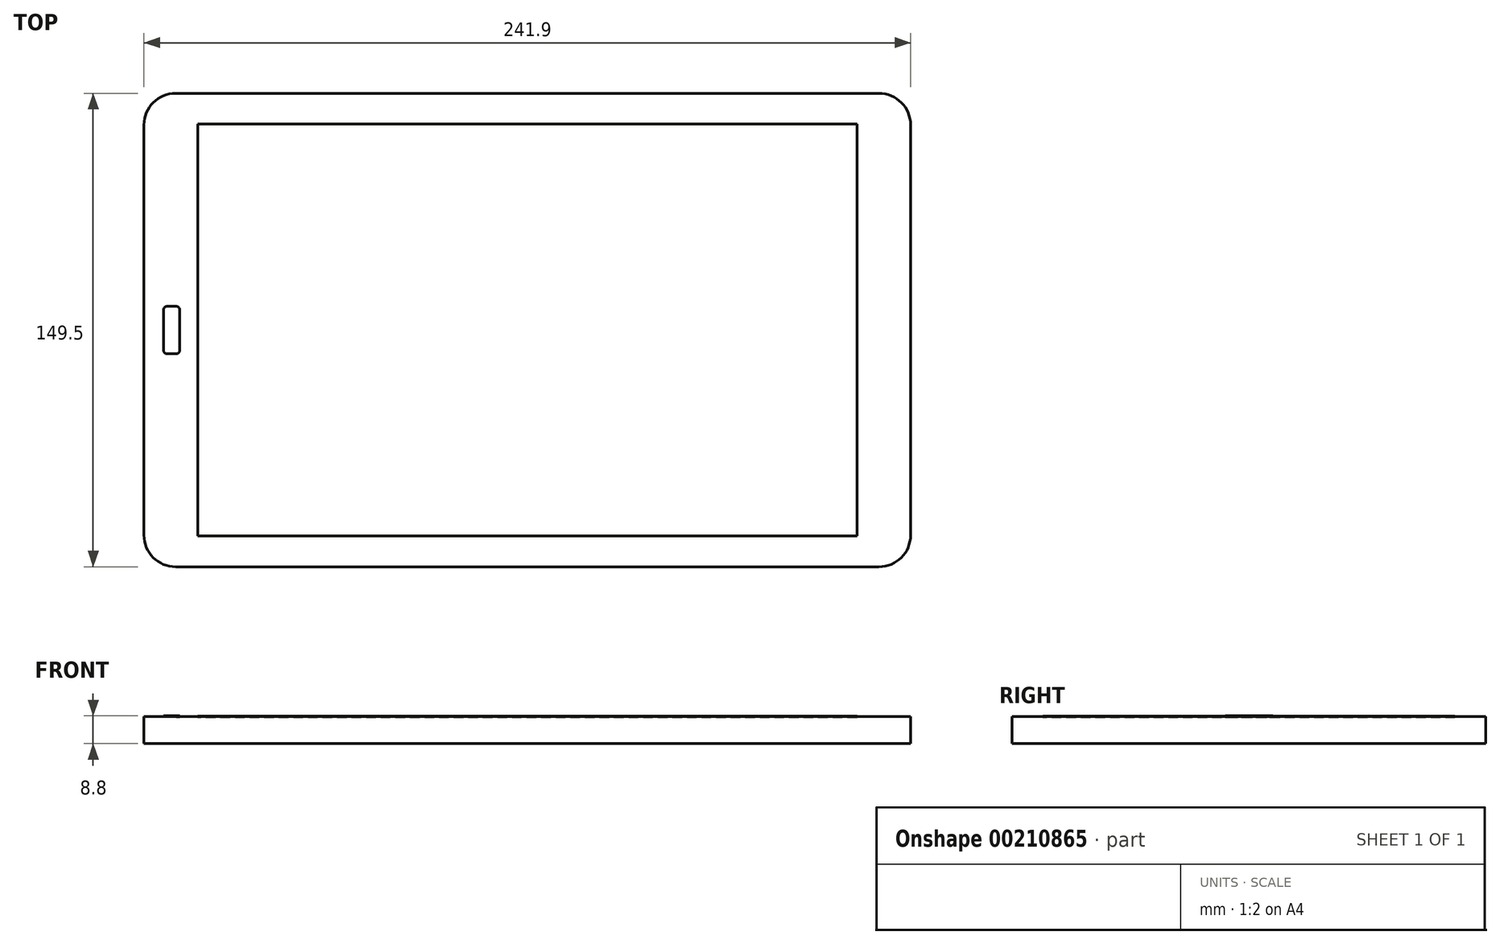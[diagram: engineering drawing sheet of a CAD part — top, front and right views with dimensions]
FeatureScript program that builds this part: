
annotation { "Feature Type Name" : "Feature", "Feature Type Description" : "" }
export const myFeature = defineFeature(function(context is Context, id is Id, definition is map)
    precondition{}
    {
        {
            var Q0;
            Q0=qCreatedBy(makeId("Top.planeOp"),FACE);
            var sketch = newSketch(context, id + "F0", { "sketchPlane" : qUnion([Q0])});
            skLineSegment(sketch, "E0.bottom", {"start": v(110.95, 74.75) * mm, "end": v(-110.95, 74.75) * mm});
            skLineSegment(sketch, "E0.top", {"start": v(110.95, -74.75) * mm, "end": v(-110.95, -74.75) * mm});
            skLineSegment(sketch, "E0.left", {"start": v(120.95, 64.75) * mm, "end": v(120.95, -64.75) * mm});
            skLineSegment(sketch, "E0.right", {"start": v(-120.95, 64.75) * mm, "end": v(-120.95, -64.75) * mm});
            skPoint(sketch, "E0.middle", {"position": v(0, 0) * mm});
            skPoint(sketch, "E1.visualSharp", {"position": v(-120.95, 74.75) * mm});
            skArc(sketch, "E1.filletArc", {"start": v(-110.95, 74.75) * mm, "mid": v(-118.02, 71.82) * mm, "end": v(-120.95, 64.75) * mm});
            skPoint(sketch, "E2.visualSharp", {"position": v(120.95, 74.75) * mm});
            skArc(sketch, "E2.filletArc", {"start": v(120.95, 64.75) * mm, "mid": v(118.02, 71.82) * mm, "end": v(110.95, 74.75) * mm});
            skPoint(sketch, "E3.visualSharp", {"position": v(120.95, -74.75) * mm});
            skArc(sketch, "E3.filletArc", {"start": v(110.95, -74.75) * mm, "mid": v(118.02, -71.82) * mm, "end": v(120.95, -64.75) * mm});
            skPoint(sketch, "E4.visualSharp", {"position": v(-120.95, -74.75) * mm});
            skArc(sketch, "E4.filletArc", {"start": v(-120.95, -64.75) * mm, "mid": v(-118.02, -71.82) * mm, "end": v(-110.95, -74.75) * mm});
            skSolve(sketch);
        }
        {
            var Q0;
            Q0=makeQuery(id+"F0.imprint","IMPRINT",FACE,{"disambiguationData":[TD([[makeQuery(id+"F0.imprint","IMPRINT",EDGE,{"derivedFrom":sQuery(id+"F0.wireOp",EDGE,"E0.bottom")}),1.0]])]});
            extrude(context, id + "F1", {"entities" : qUnion([Q0]), "depth" : 8.5 * mm});
        }
        {
            var Q0;
            Q0=qCreatedBy(makeId("Top.planeOp"),FACE);
            cPlane(context, id + "F2", {"entities" : qUnion([Q0]), "cplaneType" : CPlaneType.OFFSET, "offset" : 25 * mm, "width" : 150 * mm, "height" : 150 * mm});
        }
        {
            var Q0;
            Q0=qCreatedBy(id+"F2.planeOp",FACE);
            var sketch = newSketch(context, id + "F3", { "sketchPlane" : qUnion([Q0])});
            skLineSegment(sketch, "E5.bottom", {"start": v(104, 65) * mm, "end": v(-104, 65) * mm});
            skLineSegment(sketch, "E5.top", {"start": v(104, -65) * mm, "end": v(-104, -65) * mm});
            skLineSegment(sketch, "E5.left", {"start": v(104, 65) * mm, "end": v(104, -65) * mm});
            skLineSegment(sketch, "E5.right", {"start": v(-104, 65) * mm, "end": v(-104, -65) * mm});
            skPoint(sketch, "E5.middle", {"position": v(0, 0) * mm});
            skSolve(sketch);
        }
        {
            var Q0;
            Q0=makeQuery(id+"F3.imprint","IMPRINT",FACE,{"disambiguationData":[TD([[makeQuery(id+"F3.imprint","IMPRINT",EDGE,{"derivedFrom":sQuery(id+"F3.wireOp",EDGE,"E5.bottom")}),1.0]])]});
            extrude(context, id + "F4", {"entities" : qUnion([Q0]), "depth" : .5 * mm});
        }
        {
            var Q0;
            Q0=makeQuery(id+"F4.opExtrude","SWEPT_BODY",BODY,{"disambiguationData":[OSD([sQuery(id+"F3.wireOp",EDGE,"E5.bottom"),sQuery(id+"F3.wireOp",EDGE,"E5.top"),sQuery(id+"F3.wireOp",EDGE,"E5.left"),sQuery(id+"F3.wireOp",EDGE,"E5.right")])]});
            transform(context, id + "F5", {"entities" : qUnion([Q0]), "transformType" : TransformType.TRANSLATION_3D, "dx" : 0 * mm, "dy" : 0 * mm, "dz" : -16.9 * mm, "makeCopy" : false});
        }
        {
            var Q0;
            Q0=qCreatedBy(id+"F2.planeOp",FACE);
            var sketch = newSketch(context, id + "F6", { "sketchPlane" : qUnion([Q0])});
            skLineSegment(sketch, "E6.bottom", {"start": v(-23.52, 0) * mm, "end": v(-26.52, 0) * mm});
            skLineSegment(sketch, "E6.top", {"start": v(-23.52, 15) * mm, "end": v(-26.52, 15) * mm});
            skLineSegment(sketch, "E6.left", {"start": v(-22.52, 1) * mm, "end": v(-22.52, 14) * mm});
            skLineSegment(sketch, "E6.right", {"start": v(-27.52, 1) * mm, "end": v(-27.52, 14) * mm});
            skPoint(sketch, "E6.middle", {"position": v(-25.02, 7.5) * mm});
            skPoint(sketch, "E7.visualSharp", {"position": v(-22.52, 15) * mm});
            skArc(sketch, "E7.filletArc", {"start": v(-22.52, 14) * mm, "mid": v(-22.81, 14.7) * mm, "end": v(-23.52, 15) * mm});
            skPoint(sketch, "E8.visualSharp", {"position": v(-22.52, 0) * mm});
            skArc(sketch, "E8.filletArc", {"start": v(-23.52, 0) * mm, "mid": v(-22.81, 0.3) * mm, "end": v(-22.52, 1) * mm});
            skPoint(sketch, "E9.visualSharp", {"position": v(-27.52, 0) * mm});
            skArc(sketch, "E9.filletArc", {"start": v(-27.52, 1) * mm, "mid": v(-27.23, 0.3) * mm, "end": v(-26.52, 0) * mm});
            skPoint(sketch, "E10.visualSharp", {"position": v(-27.52, 15) * mm});
            skArc(sketch, "E10.filletArc", {"start": v(-26.52, 15) * mm, "mid": v(-27.23, 14.7) * mm, "end": v(-27.52, 14) * mm});
            skSolve(sketch);
        }
        {
            var Q0;
            Q0=makeQuery(id+"F6.imprint","IMPRINT",FACE,{"disambiguationData":[TD([[makeQuery(id+"F6.imprint","IMPRINT",EDGE,{"derivedFrom":sQuery(id+"F6.wireOp",EDGE,"E6.bottom")}),-1.0]])]});
            extrude(context, id + "F7", {"entities" : qUnion([Q0]), "depth" : .5 * mm});
        }
        {
            var Q0;
            Q0=makeQuery(id+"F7.opExtrude","SWEPT_BODY",BODY,{"disambiguationData":[OSD([sQuery(id+"F6.wireOp",EDGE,"E6.bottom"),sQuery(id+"F6.wireOp",EDGE,"E6.top"),sQuery(id+"F6.wireOp",EDGE,"E6.left"),sQuery(id+"F6.wireOp",EDGE,"E6.right"),sQuery(id+"F6.wireOp",EDGE,"E7.filletArc"),sQuery(id+"F6.wireOp",EDGE,"E8.filletArc"),sQuery(id+"F6.wireOp",EDGE,"E9.filletArc"),sQuery(id+"F6.wireOp",EDGE,"E10.filletArc")])]});
            transform(context, id + "F8", {"entities" : qUnion([Q0]), "transformType" : TransformType.TRANSLATION_3D, "dx" : -87.2 * mm, "dy" : -7.5 * mm, "dz" : -16.7 * mm, "makeCopy" : false});
        }
    });
